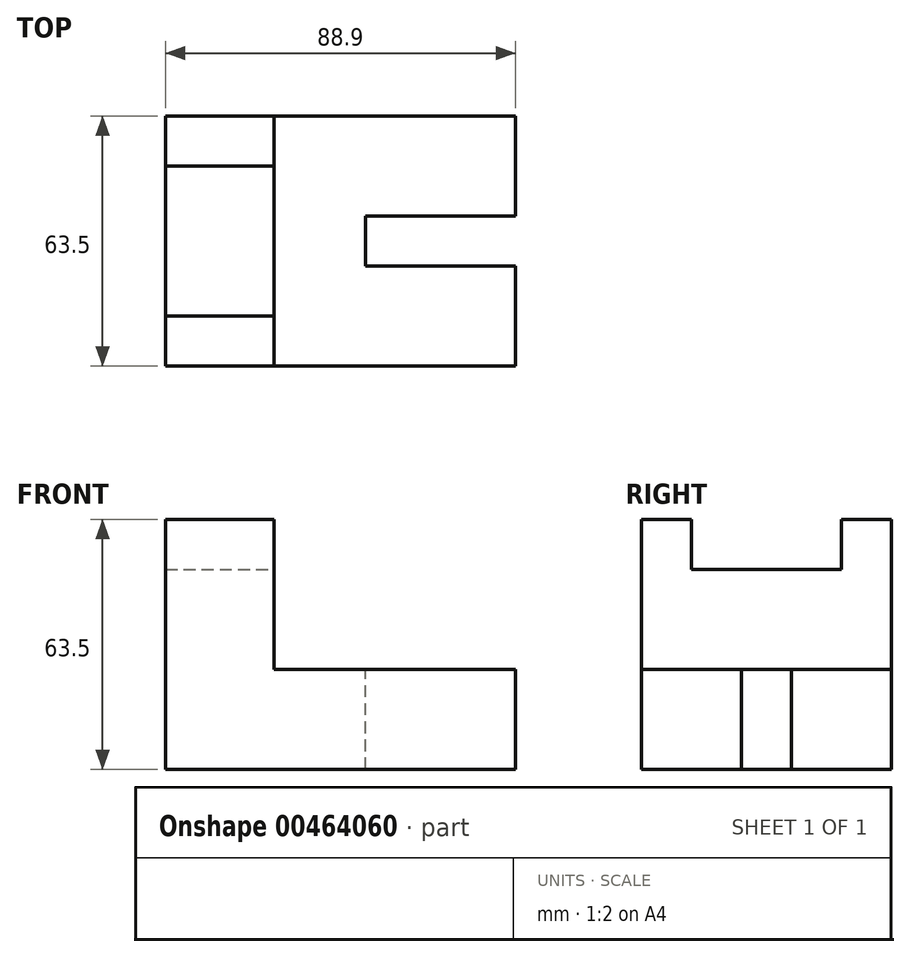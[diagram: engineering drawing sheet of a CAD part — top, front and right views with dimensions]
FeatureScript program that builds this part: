
annotation { "Feature Type Name" : "Feature", "Feature Type Description" : "" }
export const myFeature = defineFeature(function(context is Context, id is Id, definition is map)
    precondition{}
    {
        {
            var Q0;
            Q0=qCreatedBy(makeId("Front.planeOp"),FACE);
            var sketch = newSketch(context, id + "F0", { "sketchPlane" : qUnion([Q0])});
            skLineSegment(sketch, "E0", {"start": v(-57.69, 39.52) * mm, "end": v(-57.69, -23.98) * mm});
            skLineSegment(sketch, "E1", {"start": v(-57.69, -23.98) * mm, "end": v(31.21, -23.98) * mm});
            skLineSegment(sketch, "E2", {"start": v(31.21, -23.98) * mm, "end": v(31.21, 1.42) * mm});
            skLineSegment(sketch, "E3", {"start": v(31.21, 1.42) * mm, "end": v(-30.1, 1.42) * mm});
            skLineSegment(sketch, "E4", {"start": v(-30.1, 1.42) * mm, "end": v(-30.1, 39.52) * mm});
            skLineSegment(sketch, "E5", {"start": v(-30.1, 39.52) * mm, "end": v(-57.69, 39.52) * mm});
            skSolve(sketch);
        }
        {
            var Q0;
            Q0=makeQuery(id+"F0.imprint","IMPRINT",FACE,{"disambiguationData":[TD([[makeQuery(id+"F0.imprint","IMPRINT",EDGE,{"derivedFrom":sQuery(id+"F0.wireOp",EDGE,"E0")}),1.0]])]});
            extrude(context, id + "F1", {"entities" : qUnion([Q0]), "depth" : 63.5 * mm});
        }
        {
            var Q0;
            Q0=makeQuery(id+"F1.opExtrude","SWEPT_FACE",FACE,{"disambiguationData":[OSD([sQuery(id+"F0.wireOp",EDGE,"E4")])]});
            var sketch = newSketch(context, id + "F2", { "sketchPlane" : qUnion([Q0])});
            skLineSegment(sketch, "E6", {"start": v(-50.8, 39.52) * mm, "end": v(-50.8, 26.82) * mm});
            skLineSegment(sketch, "E7", {"start": v(-50.8, 26.82) * mm, "end": v(-12.7, 26.82) * mm});
            skLineSegment(sketch, "E8", {"start": v(-12.7, 26.82) * mm, "end": v(-12.7, 39.52) * mm});
            skLineSegment(sketch, "E9", {"start": v(-12.7, 39.52) * mm, "end": v(-50.8, 39.52) * mm});
            skSolve(sketch);
        }
        {
            var Q0;
            Q0=makeQuery(id+"F2.imprint","IMPRINT",FACE,{"disambiguationData":[TD([[makeQuery(id+"F2.imprint","IMPRINT",EDGE,{"derivedFrom":sQuery(id+"F2.wireOp",EDGE,"E6")}),1.0]])]});
            extrude(context, id + "F3", {"entities" : qUnion([Q0]), "operationType" : NewBodyOperationType.REMOVE, "endBound" : BoundingType.THROUGH_ALL, "oppositeDirection" : true, "depth" : 25.4 * mm});
        }
        {
            var Q0;
            Q0=makeQuery(id+"F1.opExtrude","SWEPT_FACE",FACE,{"disambiguationData":[OSD([sQuery(id+"F0.wireOp",EDGE,"E3")])]});
            var sketch = newSketch(context, id + "F4", { "sketchPlane" : qUnion([Q0])});
            skLineSegment(sketch, "E10", {"start": v(31.21, -25.4) * mm, "end": v(-6.89, -25.4) * mm});
            skLineSegment(sketch, "E11", {"start": v(-6.89, -25.4) * mm, "end": v(-6.89, -38.1) * mm});
            skLineSegment(sketch, "E12", {"start": v(-6.89, -38.1) * mm, "end": v(31.21, -38.1) * mm});
            skSolve(sketch);
        }
        {
            var Q0;
            {var subQ0=sQuery(id+"F4.wireOp",EDGE,"E10");Q0=makeQuery(id+"F4.imprint","IMPRINT",FACE,{"disambiguationData":[TD([[makeQuery(id+"F4.imprint","IMPRINT",EDGE,{"derivedFrom":subQ0}),1.0]])]});}
            extrude(context, id + "F5", {"entities" : qUnion([Q0]), "operationType" : NewBodyOperationType.REMOVE, "endBound" : BoundingType.THROUGH_ALL, "oppositeDirection" : true, "depth" : 25.4 * mm});
        }
    });
